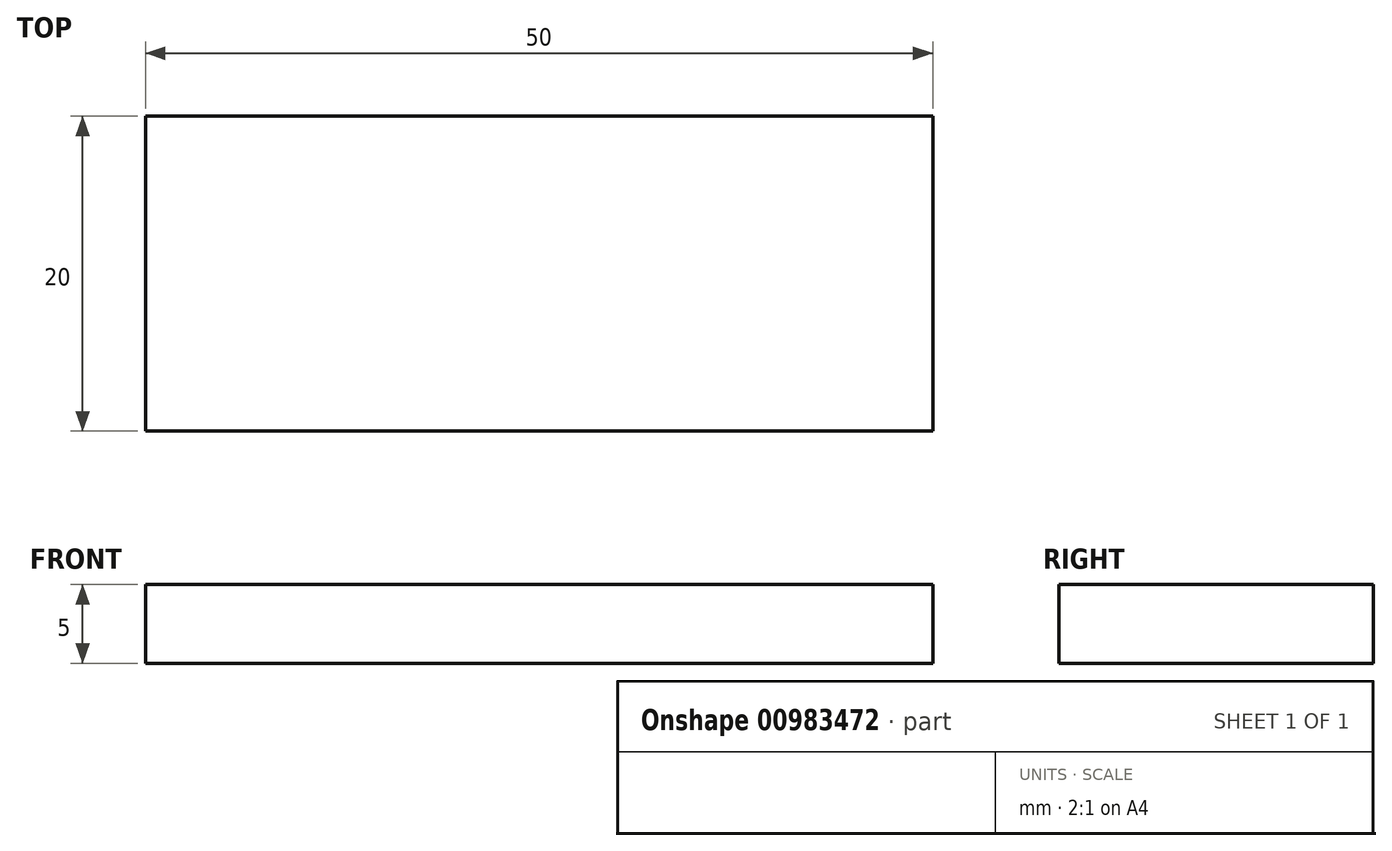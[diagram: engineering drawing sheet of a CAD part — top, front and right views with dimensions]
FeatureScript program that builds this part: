
annotation { "Feature Type Name" : "Feature", "Feature Type Description" : "" }
export const myFeature = defineFeature(function(context is Context, id is Id, definition is map)
    precondition{}
    {
        {
            var Q0;
            Q0=qCreatedBy(makeId("Top.planeOp"),FACE);
            var sketch = newSketch(context, id + "F0", { "sketchPlane" : qUnion([Q0])});
            skLineSegment(sketch, "E0.bottom", {"start": v(25, 10) * mm, "end": v(-25, 10) * mm});
            skLineSegment(sketch, "E0.top", {"start": v(25, -10) * mm, "end": v(-25, -10) * mm});
            skLineSegment(sketch, "E0.left", {"start": v(25, 10) * mm, "end": v(25, -10) * mm});
            skLineSegment(sketch, "E0.right", {"start": v(-25, 10) * mm, "end": v(-25, -10) * mm});
            skPoint(sketch, "E0.middle", {"position": v(0, 0) * mm});
            skSolve(sketch);
        }
        {
            var Q0;
            Q0=makeQuery(id+"F0.imprint","IMPRINT",FACE,{"disambiguationData":[TD([[makeQuery(id+"F0.imprint","IMPRINT",EDGE,{"derivedFrom":sQuery(id+"F0.wireOp",EDGE,"E0.bottom")}),1.0]])]});
            extrude(context, id + "F1", {"entities" : qUnion([Q0]), "depth" : 5 * mm, "offsetDistance" : 25 * mm});
        }
    });
